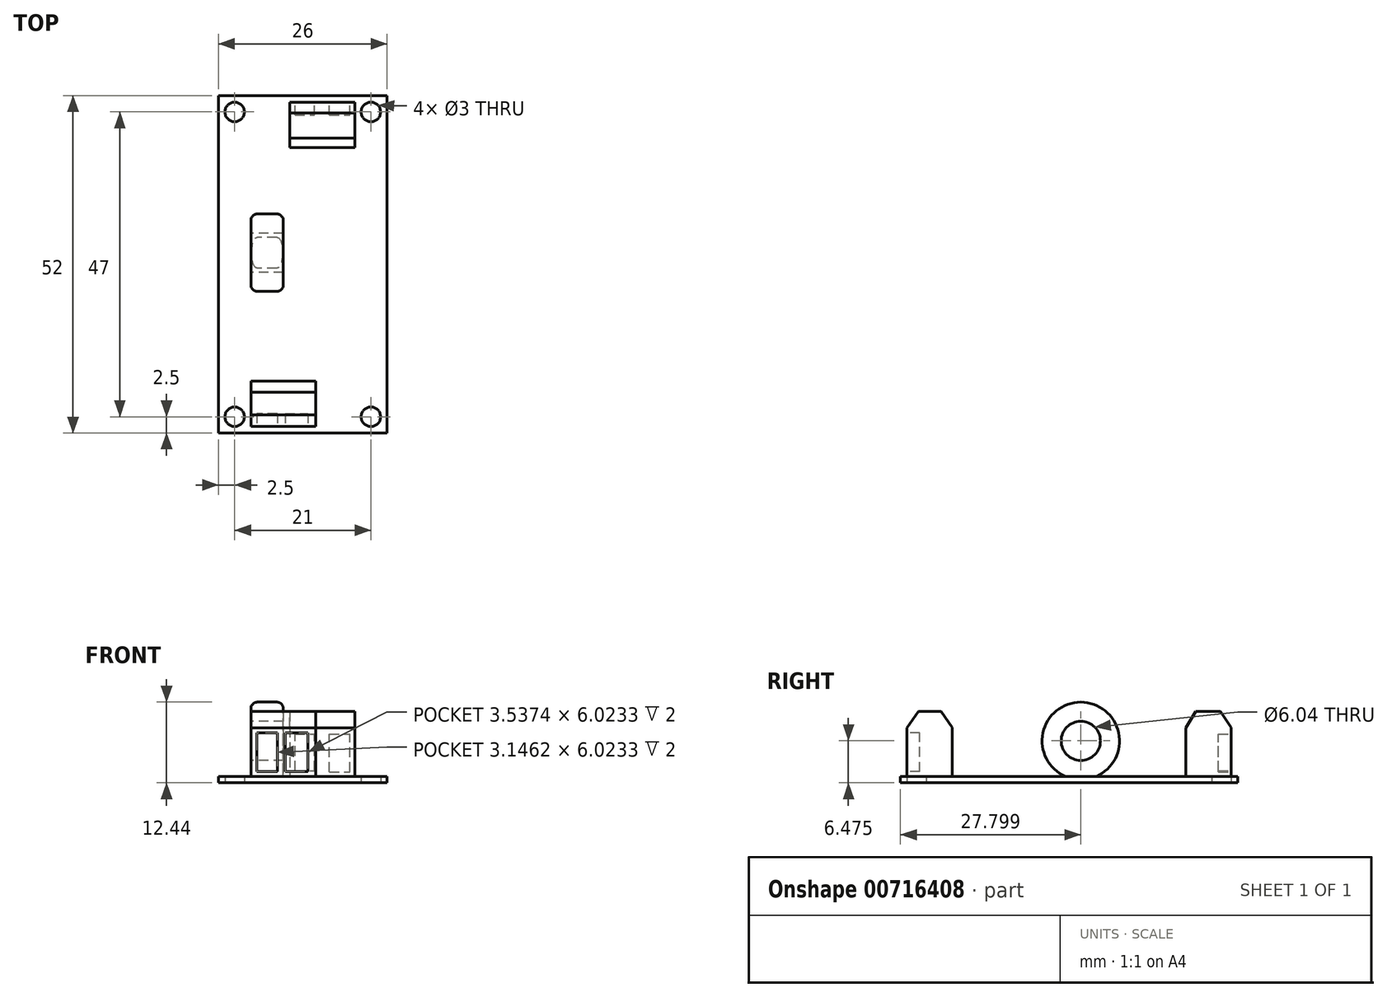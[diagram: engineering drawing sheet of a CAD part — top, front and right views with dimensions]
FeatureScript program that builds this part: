
annotation { "Feature Type Name" : "Feature", "Feature Type Description" : "" }
export const myFeature = defineFeature(function(context is Context, id is Id, definition is map)
    precondition{}
    {
        {
            var Q0;
            Q0=qCreatedBy(makeId("Top.planeOp"),FACE);
            var sketch = newSketch(context, id + "F0", { "sketchPlane" : qUnion([Q0])});
            skLineSegment(sketch, "E0.bottom", {"start": v(0, 0) * mm, "end": v(26, 0) * mm});
            skLineSegment(sketch, "E0.top", {"start": v(0, 52) * mm, "end": v(26, 52) * mm});
            skLineSegment(sketch, "E0.left", {"start": v(0, 0) * mm, "end": v(0, 52) * mm});
            skLineSegment(sketch, "E0.right", {"start": v(26, 0) * mm, "end": v(26, 52) * mm});
            skLineSegment(sketch, "E1", {"start": v(13, 52) * mm, "end": v(13, 0) * mm, "construction": true});
            skLineSegment(sketch, "E2", {"start": v(0, 26) * mm, "end": v(26, 26) * mm, "construction": true});
            skCircle(sketch, "E3", {"center": v(2.5, 2.5) * mm, "radius": 1.5 * mm});
            skCircle(sketch, "E4.MirrorC", {"center": v(23.5, 2.5) * mm, "radius": 1.5 * mm});
            skLineSegment(sketch, "E5.MirrorCS", {"start": v(26, 0) * mm, "end": v(0, 0) * mm});
            skCircle(sketch, "E6.MirrorC", {"center": v(23.5, 49.5) * mm, "radius": 1.5 * mm});
            skCircle(sketch, "E7.MirrorC", {"center": v(2.5, 49.5) * mm, "radius": 1.5 * mm});
            skSolve(sketch);
        }
        {
            var Q0;
            Q0 = qSketchRegion(id + "F0", true);
            extrude(context, id + "F1", {"entities" : qUnion([Q0]), "depth" : 1 * mm, "offsetDistance" : 25 * mm});
        }
        {
            var Q0;
            Q0=makeQuery(id+"F1.opExtrude","CAP_FACE",FACE,{"disambiguationData":[OSD([sQuery(id+"F0.wireOp",EDGE,"E0.top"),sQuery(id+"F0.wireOp",EDGE,"E0.left"),sQuery(id+"F0.wireOp",EDGE,"E0.right"),sQuery(id+"F0.wireOp",EDGE,"E3"),sQuery(id+"F0.wireOp",EDGE,"E5.MirrorCS"),sQuery(id+"F0.wireOp",EDGE,"E4.MirrorC"),sQuery(id+"F0.wireOp",EDGE,"E6.MirrorC"),sQuery(id+"F0.wireOp",EDGE,"E7.MirrorC")])],"isStart":false});
            var sketch = newSketch(context, id + "F2", { "sketchPlane" : qUnion([Q0])});
            skLineSegment(sketch, "E8.bottom", {"start": v(15, 1) * mm, "end": v(5, 1) * mm});
            skLineSegment(sketch, "E8.top", {"start": v(15, 8) * mm, "end": v(5, 8) * mm});
            skLineSegment(sketch, "E8.left", {"start": v(15, 1) * mm, "end": v(15, 8) * mm});
            skLineSegment(sketch, "E8.right", {"start": v(5, 1) * mm, "end": v(5, 8) * mm});
            skPoint(sketch, "E8.middle", {"position": v(10, 4.5) * mm});
            skLineSegment(sketch, "E9.bottom", {"start": v(21, 44) * mm, "end": v(11, 44) * mm});
            skLineSegment(sketch, "E9.top", {"start": v(21, 51) * mm, "end": v(11, 51) * mm});
            skLineSegment(sketch, "E9.left", {"start": v(21, 44) * mm, "end": v(21, 51) * mm});
            skLineSegment(sketch, "E9.right", {"start": v(11, 44) * mm, "end": v(11, 51) * mm});
            skPoint(sketch, "E9.middle", {"position": v(16, 47.5) * mm});
            skSolve(sketch);
        }
        {
            var Q0;
            Q0 = qSketchRegion(id + "F2", true);
            extrude(context, id + "F3", {"entities" : qUnion([Q0]), "operationType" : NewBodyOperationType.ADD, "depth" : 10 * mm, "offsetDistance" : 25 * mm});
        }
        {
            var Q0;
            Q0=makeQuery(id+"F3.opExtrude","SWEPT_FACE",FACE,{"disambiguationData":[OSD([sQuery(id+"F2.wireOp",EDGE,"E9.left")])]});
            var sketch = newSketch(context, id + "F4", { "sketchPlane" : qUnion([Q0])});
            skLineSegment(sketch, "E10", {"start": v(49.34, 11) * mm, "end": v(51, 8.56) * mm});
            skLineSegment(sketch, "E11", {"start": v(51, 8.56) * mm, "end": v(51, 11) * mm});
            skLineSegment(sketch, "E12", {"start": v(51, 11) * mm, "end": v(49.34, 11) * mm});
            skLineSegment(sketch, "E13", {"start": v(44, 11) * mm, "end": v(44, 8.5) * mm});
            skLineSegment(sketch, "E14", {"start": v(44, 8.5) * mm, "end": v(45.48, 11) * mm});
            skLineSegment(sketch, "E15", {"start": v(45.48, 11) * mm, "end": v(44, 11) * mm});
            skLineSegment(sketch, "E16", {"start": v(0.99, 11) * mm, "end": v(0.99, 8.43) * mm});
            skLineSegment(sketch, "E17", {"start": v(0.99, 8.43) * mm, "end": v(2.77, 11) * mm});
            skLineSegment(sketch, "E18", {"start": v(2.77, 11) * mm, "end": v(0.99, 11) * mm});
            skLineSegment(sketch, "E19", {"start": v(6.26, 11) * mm, "end": v(8.08, 8.43) * mm});
            skLineSegment(sketch, "E20", {"start": v(8.08, 8.43) * mm, "end": v(8.08, 11) * mm});
            skLineSegment(sketch, "E21", {"start": v(8.08, 11) * mm, "end": v(6.26, 11) * mm});
            skSolve(sketch);
        }
        {
            var Q0;
            Q0 = qSketchRegion(id + "F4", true);
            extrude(context, id + "F5", {"entities" : qUnion([Q0]), "operationType" : NewBodyOperationType.REMOVE, "endBound" : BoundingType.THROUGH_ALL, "oppositeDirection" : true, "depth" : 25 * mm, "offsetDistance" : 25 * mm});
        }
        {
            var Q0;
            Q0=makeQuery(id+"F3.opExtrude","SWEPT_FACE",FACE,{"disambiguationData":[OSD([sQuery(id+"F2.wireOp",EDGE,"E9.top")])]});
            var sketch = newSketch(context, id + "F6", { "sketchPlane" : qUnion([Q0])});
            skLineSegment(sketch, "E22.bottom", {"start": v(-17.1, 1.68) * mm, "end": v(-20.28, 1.68) * mm});
            skLineSegment(sketch, "E22.top", {"start": v(-17.1, 7.55) * mm, "end": v(-20.28, 7.55) * mm});
            skLineSegment(sketch, "E22.left", {"start": v(-17.1, 1.68) * mm, "end": v(-17.1, 7.55) * mm});
            skLineSegment(sketch, "E22.right", {"start": v(-20.28, 1.68) * mm, "end": v(-20.28, 7.55) * mm});
            skPoint(sketch, "E22.middle", {"position": v(-18.69, 4.61) * mm});
            skLineSegment(sketch, "E23.bottom", {"start": v(-11.8, 1.87) * mm, "end": v(-14.8, 1.87) * mm});
            skLineSegment(sketch, "E23.top", {"start": v(-11.8, 7.55) * mm, "end": v(-14.8, 7.55) * mm});
            skLineSegment(sketch, "E23.left", {"start": v(-11.8, 1.87) * mm, "end": v(-11.8, 7.55) * mm});
            skLineSegment(sketch, "E23.right", {"start": v(-14.8, 1.87) * mm, "end": v(-14.8, 7.55) * mm});
            skPoint(sketch, "E23.middle", {"position": v(-13.3, 4.7) * mm});
            skSolve(sketch);
        }
        {
            var Q0;
            Q0 = qSketchRegion(id + "F6", true);
            extrude(context, id + "F7", {"entities" : qUnion([Q0]), "operationType" : NewBodyOperationType.REMOVE, "oppositeDirection" : true, "depth" : 2 * mm, "offsetDistance" : 25 * mm});
        }
        {
            var Q0;
            Q0=makeQuery(id+"F3.opExtrude","SWEPT_FACE",FACE,{"disambiguationData":[OSD([sQuery(id+"F2.wireOp",EDGE,"E8.bottom")])]});
            var sketch = newSketch(context, id + "F8", { "sketchPlane" : qUnion([Q0])});
            skLineSegment(sketch, "E24.bottom", {"start": v(9.08, 1.71) * mm, "end": v(5.93, 1.71) * mm});
            skLineSegment(sketch, "E24.top", {"start": v(9.08, 7.74) * mm, "end": v(5.93, 7.74) * mm});
            skLineSegment(sketch, "E24.left", {"start": v(9.08, 1.71) * mm, "end": v(9.08, 7.74) * mm});
            skLineSegment(sketch, "E24.right", {"start": v(5.93, 1.71) * mm, "end": v(5.93, 7.74) * mm});
            skPoint(sketch, "E24.middle", {"position": v(7.5, 4.73) * mm});
            skPoint(sketch, "E24.middle.positionSnap0", {"position": v(5, 4.73) * mm});
            skPoint(sketch, "E24.centerSnap0", {"position": v(5, 4.73) * mm});
            skLineSegment(sketch, "E25.bottom", {"start": v(10.27, 1.71) * mm, "end": v(13.8, 1.71) * mm});
            skLineSegment(sketch, "E25.top", {"start": v(10.27, 7.74) * mm, "end": v(13.8, 7.74) * mm});
            skLineSegment(sketch, "E25.left", {"start": v(10.27, 1.71) * mm, "end": v(10.27, 7.74) * mm});
            skLineSegment(sketch, "E25.right", {"start": v(13.8, 1.71) * mm, "end": v(13.8, 7.74) * mm});
            skPoint(sketch, "E25.middle", {"position": v(12.04, 4.73) * mm});
            skSolve(sketch);
        }
        {
            var Q0;
            Q0 = qSketchRegion(id + "F8", true);
            extrude(context, id + "F9", {"entities" : qUnion([Q0]), "operationType" : NewBodyOperationType.REMOVE, "oppositeDirection" : true, "depth" : 2 * mm, "offsetDistance" : 25 * mm});
        }
        {
            var Q0;
            Q0=qCreatedBy(makeId("Right.planeOp"),FACE);
            cPlane(context, id + "F10", {"entities" : qUnion([Q0]), "cplaneType" : CPlaneType.OFFSET, "offset" : 5 * mm, "width" : 150 * mm, "height" : 150 * mm});
        }
        {
            var Q0;
            Q0=qCreatedBy(id+"F10.planeOp",FACE);
            var sketch = newSketch(context, id + "F11", { "sketchPlane" : qUnion([Q0])});
            skCircle(sketch, "E26", {"center": v(27.8, 6.47) * mm, "radius": 5.97 * mm});
            skCircle(sketch, "E27", {"center": v(27.8, 6.47) * mm, "radius": 3.02 * mm});
            skSolve(sketch);
        }
        {
            var Q0;
            Q0 = qSketchRegion(id + "F11", true);
            extrude(context, id + "F12", {"entities" : qUnion([Q0]), "operationType" : NewBodyOperationType.ADD, "depth" : 5 * mm, "offsetDistance" : 25 * mm});
        }
        {
            var Q0;
            Q0=makeQuery(id+"F12.opExtrude","CAP_EDGE",EDGE,{"disambiguationData":[OSD([sQuery(id+"F11.wireOp",EDGE,"E26")])],"isStart":false});
            var Q1;
            Q1=makeQuery(id+"F12.opExtrude","CAP_EDGE",EDGE,{"disambiguationData":[OSD([sQuery(id+"F11.wireOp",EDGE,"E26")])],"isStart":true});
            fillet(context, id + "F13", {"entities" : qUnion([Q0, Q1]), "radius" : 1 * mm, "tangentPropagation" : true, "allowEdgeOverflow" : false});
        }
    });
